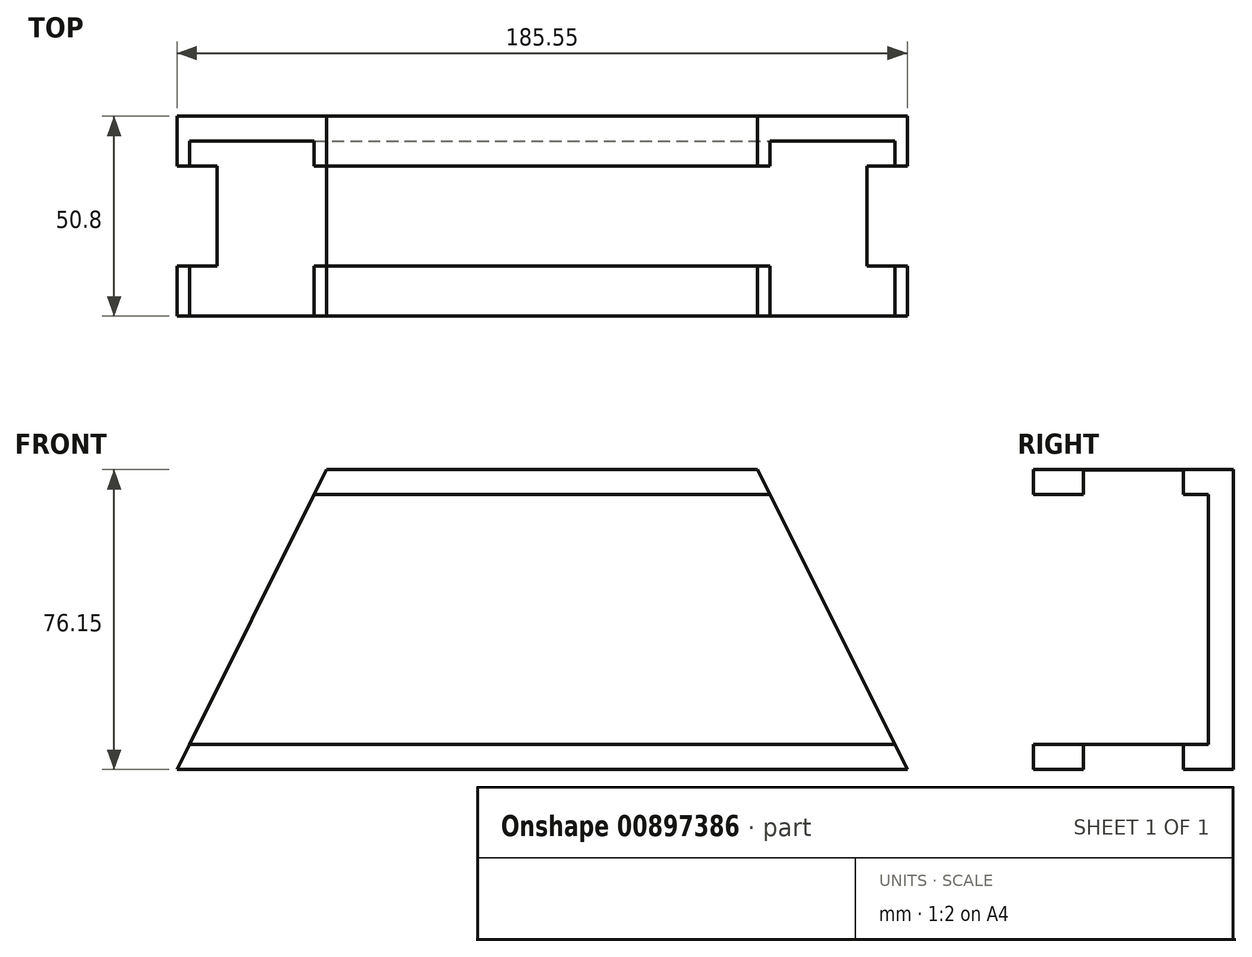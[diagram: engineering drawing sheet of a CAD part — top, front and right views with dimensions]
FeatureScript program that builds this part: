
annotation { "Feature Type Name" : "Feature", "Feature Type Description" : "" }
export const myFeature = defineFeature(function(context is Context, id is Id, definition is map)
    precondition{}
    {
        {
            var Q0;
            Q0=qCreatedBy(makeId("Front.planeOp"),FACE);
            var sketch = newSketch(context, id + "F0", { "sketchPlane" : qUnion([Q0])});
            skLineSegment(sketch, "E0", {"start": v(-50.8, 27.38) * mm, "end": v(50.8, 27.38) * mm});
            skLineSegment(sketch, "E1", {"start": v(-82.55, -36.12) * mm, "end": v(82.55, -36.12) * mm});
            skLineSegment(sketch, "E2", {"start": v(-50.8, 27.38) * mm, "end": v(-82.55, -36.12) * mm});
            skLineSegment(sketch, "E3", {"start": v(50.8, 27.38) * mm, "end": v(82.55, -36.12) * mm});
            skLineSegment(sketch, "E4.0", {"start": v(-54.72, 33.73) * mm, "end": v(-92.82, -42.47) * mm});
            skLineSegment(sketch, "E4.1", {"start": v(-54.72, 33.73) * mm, "end": v(54.72, 33.73) * mm});
            skLineSegment(sketch, "E4.2", {"start": v(54.72, 33.73) * mm, "end": v(92.82, -42.47) * mm});
            skLineSegment(sketch, "E4.3", {"start": v(-92.82, -42.47) * mm, "end": v(92.82, -42.47) * mm});
            skLineSegment(sketch, "E5", {"start": v(-47.63, 27.38) * mm, "end": v(-47.63, -36.12) * mm});
            skLineSegment(sketch, "E6.0", {"start": v(-53.98, 21.03) * mm, "end": v(-53.98, -36.12) * mm});
            skLineSegment(sketch, "E7.MirrorCS", {"start": v(47.63, 27.38) * mm, "end": v(47.63, -36.12) * mm});
            skLineSegment(sketch, "E8.MirrorCS", {"start": v(53.98, 21.03) * mm, "end": v(53.98, -36.12) * mm});
            skLineSegment(sketch, "E9", {"start": v(-47.63, 27.38) * mm, "end": v(0, -36.12) * mm});
            skLineSegment(sketch, "E10", {"start": v(-7.94, -36.12) * mm, "end": v(-47.62, 16.8) * mm});
            skLineSegment(sketch, "E11.bottom", {"start": v(-3.17, -36.12) * mm, "end": v(3.18, -36.12) * mm});
            skLineSegment(sketch, "E11.top", {"start": v(-3.18, 27.38) * mm, "end": v(3.17, 27.38) * mm});
            skLineSegment(sketch, "E11.left", {"start": v(-3.17, -36.12) * mm, "end": v(-3.18, 27.38) * mm});
            skLineSegment(sketch, "E11.right", {"start": v(3.18, -36.12) * mm, "end": v(3.17, 27.38) * mm});
            skLineSegment(sketch, "E12.MirrorCS", {"start": v(7.94, -36.12) * mm, "end": v(47.62, 16.8) * mm});
            skLineSegment(sketch, "E13.MirrorCS", {"start": v(47.63, 27.38) * mm, "end": v(0, -36.12) * mm});
            skLineSegment(sketch, "E14.bottom", {"start": v(47.63, -7.54) * mm, "end": v(-47.63, -7.54) * mm});
            skLineSegment(sketch, "E14.top", {"start": v(47.63, -1.2) * mm, "end": v(-47.63, -1.2) * mm});
            skLineSegment(sketch, "E14.left", {"start": v(47.63, -7.54) * mm, "end": v(47.63, -1.2) * mm});
            skLineSegment(sketch, "E14.right", {"start": v(-47.63, -7.54) * mm, "end": v(-47.63, -1.2) * mm});
            skPoint(sketch, "E14.middle", {"position": v(0, -4.37) * mm});
            skSolve(sketch);
        }
        {
            var Q0;
            Q0=qCreatedBy(makeId("Front.planeOp"),FACE);
            var sketch = newSketch(context, id + "F1", { "sketchPlane" : qUnion([Q0])});
            skLineSegment(sketch, "E15", {"start": v(-54.72, 33.73) * mm, "end": v(54.72, 33.73) * mm});
            skLineSegment(sketch, "E16", {"start": v(54.72, 33.73) * mm, "end": v(92.8, -42.42) * mm});
            skLineSegment(sketch, "E17", {"start": v(92.8, -42.42) * mm, "end": v(-92.74, -42.42) * mm});
            skLineSegment(sketch, "E18", {"start": v(-92.74, -42.42) * mm, "end": v(-54.72, 33.73) * mm});
            skSolve(sketch);
        }
        {
            var Q0;
            Q0 = qSketchRegion(id + "F1", true);
            extrude(context, id + "F2", {"entities" : qUnion([Q0]), "endBound" : BoundingType.SYMMETRIC, "depth" : 76.2 * mm, "offsetDistance" : 25.4 * mm});
        }
        {
            var Q0;
            Q0=qCreatedBy(makeId("Right.planeOp"),FACE);
            var sketch = newSketch(context, id + "F3", { "sketchPlane" : qUnion([Q0])});
            skPoint(sketch, "E19.middle", {"position": v(0, 0) * mm});
            skLineSegment(sketch, "E20.bottom", {"start": v(-31.75, 27.38) * mm, "end": v(31.75, 27.38) * mm});
            skLineSegment(sketch, "E20.top", {"start": v(-31.75, -36.07) * mm, "end": v(31.75, -36.07) * mm});
            skLineSegment(sketch, "E20.left", {"start": v(-31.75, 27.38) * mm, "end": v(-31.75, -36.07) * mm});
            skLineSegment(sketch, "E20.right", {"start": v(31.75, 27.38) * mm, "end": v(31.75, -36.07) * mm});
            skSolve(sketch);
        }
        {
            var Q0;
            Q0 = qSketchRegion(id + "F3", true);
            extrude(context, id + "F4", {"entities" : qUnion([Q0]), "operationType" : NewBodyOperationType.REMOVE, "endBound" : BoundingType.SYMMETRIC, "oppositeDirection" : true, "depth" : 203.2 * mm, "offsetDistance" : 25.4 * mm});
        }
        {
            var Q0;
            Q0 = qSketchRegion(id + "F0", true);
            var Q1;
            Q1=makeQuery(id+"F2.opExtrude","CAP_FACE",FACE,{"disambiguationData":[OSD([sQuery(id+"F1.wireOp",EDGE,"E15"),sQuery(id+"F1.wireOp",EDGE,"E16"),sQuery(id+"F1.wireOp",EDGE,"E17"),sQuery(id+"F1.wireOp",EDGE,"E18")])],"isStart":false});
            extrude(context, id + "F5", {"entities" : qUnion([Q0, Q1]), "operationType" : NewBodyOperationType.REMOVE, "oppositeDirection" : true, "depth" : 25.4 * mm, "offsetDistance" : 25.4 * mm});
        }
    });
